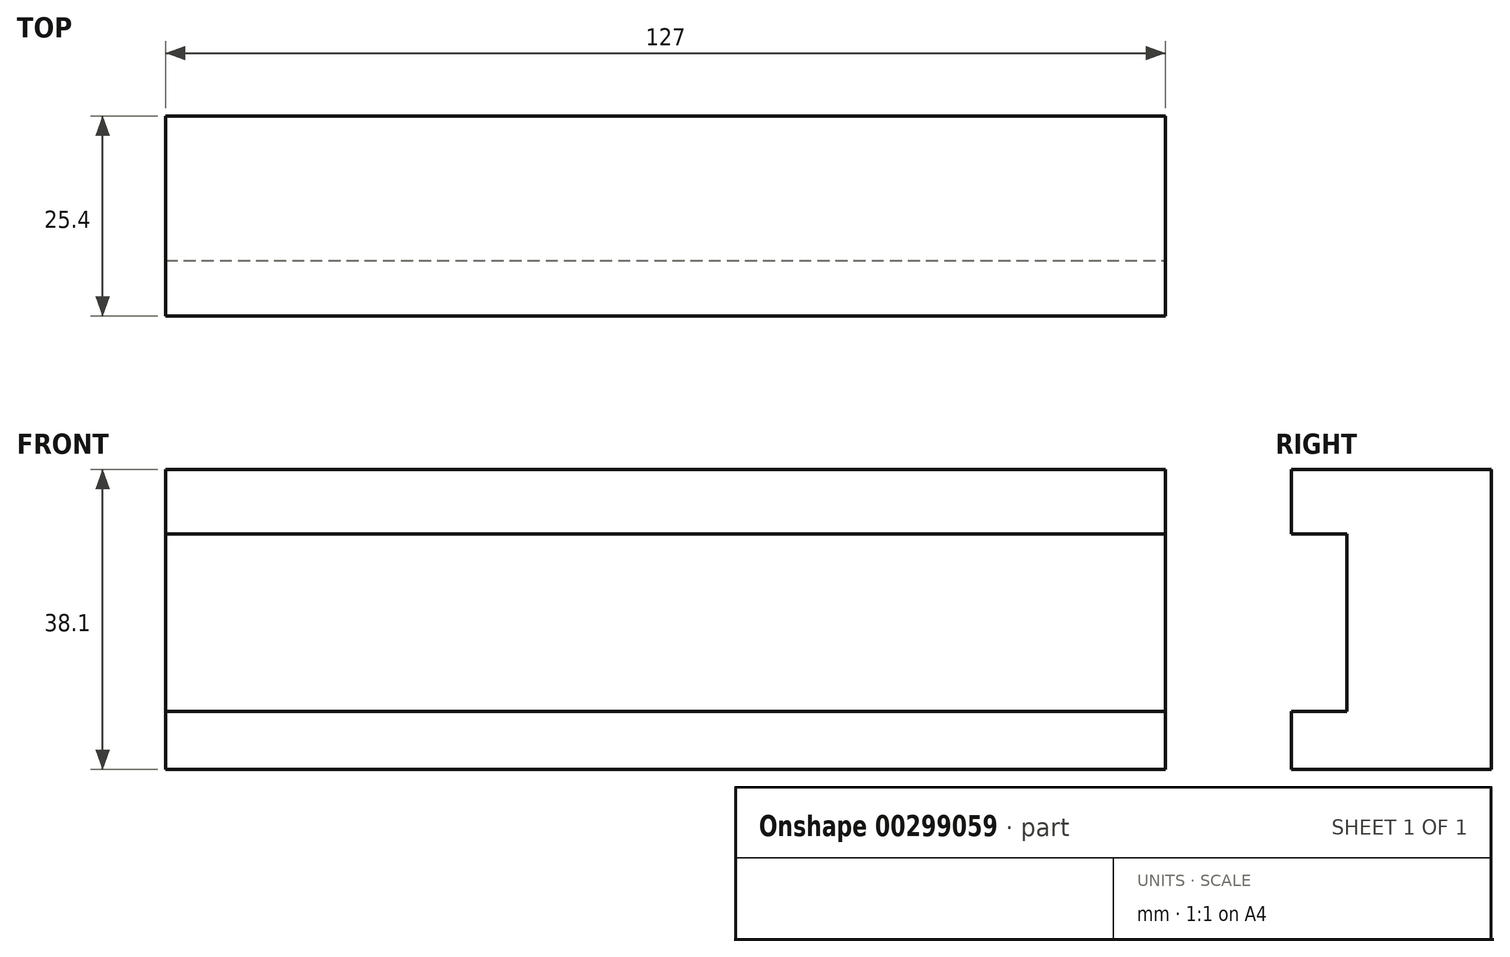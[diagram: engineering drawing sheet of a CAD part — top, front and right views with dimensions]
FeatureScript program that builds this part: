
annotation { "Feature Type Name" : "Feature", "Feature Type Description" : "" }
export const myFeature = defineFeature(function(context is Context, id is Id, definition is map)
    precondition{}
    {
        {
            var Q0;
            Q0=qCreatedBy(makeId("Front.planeOp"),FACE);
            var sketch = newSketch(context, id + "F0", { "sketchPlane" : qUnion([Q0])});
            skLineSegment(sketch, "E0.bottom", {"start": v(10.56, -23.9) * mm, "end": v(-116.44, -23.9) * mm});
            skLineSegment(sketch, "E0.top", {"start": v(10.56, 14.2) * mm, "end": v(-116.44, 14.2) * mm});
            skLineSegment(sketch, "E0.left", {"start": v(10.56, -23.9) * mm, "end": v(10.56, 14.2) * mm});
            skLineSegment(sketch, "E0.right", {"start": v(-116.44, -23.9) * mm, "end": v(-116.44, 14.2) * mm});
            skPoint(sketch, "E0.middle", {"position": v(-52.94, -4.85) * mm});
            skSolve(sketch);
        }
        {
            var Q0;
            Q0 = qSketchRegion(id + "F0", true);
            extrude(context, id + "F1", {"entities" : qUnion([Q0]), "depth" : 25.4 * mm});
        }
        {
            var Q0;
            Q0=makeQuery(id+"F1.opExtrude","SWEPT_FACE",FACE,{"disambiguationData":[OSD([sQuery(id+"F0.wireOp",EDGE,"E0.left")])]});
            var sketch = newSketch(context, id + "F2", { "sketchPlane" : qUnion([Q0])});
            skLineSegment(sketch, "E1.bottom", {"start": v(-29.17, 6.02) * mm, "end": v(-18.35, 6.02) * mm});
            skLineSegment(sketch, "E1.top", {"start": v(-29.17, -16.54) * mm, "end": v(-18.35, -16.54) * mm});
            skLineSegment(sketch, "E1.left", {"start": v(-29.17, 6.02) * mm, "end": v(-29.17, -16.54) * mm});
            skLineSegment(sketch, "E1.right", {"start": v(-18.35, 6.02) * mm, "end": v(-18.35, -16.54) * mm});
            skLineSegment(sketch, "E2.bottom", {"start": v(41.2, 43.92) * mm, "end": v(102.27, 43.92) * mm});
            skLineSegment(sketch, "E2.top", {"start": v(41.2, 18.65) * mm, "end": v(102.27, 18.65) * mm});
            skLineSegment(sketch, "E2.left", {"start": v(41.2, 43.92) * mm, "end": v(41.2, 18.65) * mm});
            skLineSegment(sketch, "E2.right", {"start": v(102.27, 43.92) * mm, "end": v(102.27, 18.65) * mm});
            skSolve(sketch);
        }
        {
            var Q0;
            {var subQ0=sQuery(id+"F2.wireOp",EDGE,"E1.right");Q0=makeQuery(id+"F2.imprint","IMPRINT",FACE,{"disambiguationData":[TD([[makeQuery(id+"F2.imprint","IMPRINT",EDGE,{"derivedFrom":subQ0}),-1.0]])]});}
            extrude(context, id + "F3", {"entities" : qUnion([Q0]), "operationType" : NewBodyOperationType.REMOVE, "oppositeDirection" : true, "depth" : 152.4 * mm});
        }
    });
